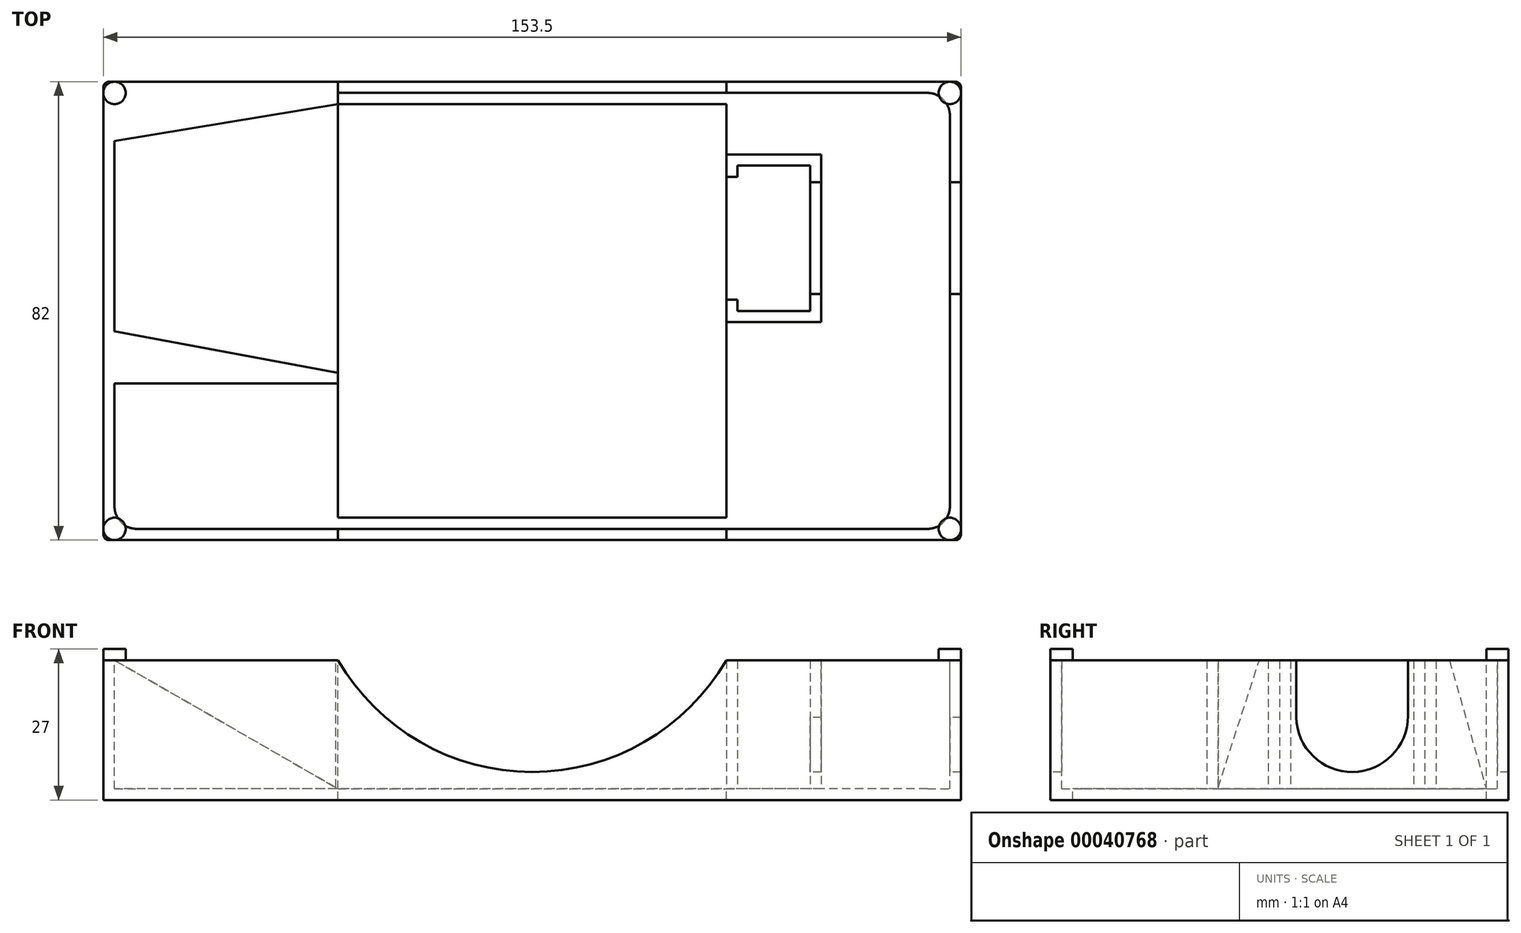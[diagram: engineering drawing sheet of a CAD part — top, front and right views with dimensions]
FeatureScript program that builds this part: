
annotation { "Feature Type Name" : "Feature", "Feature Type Description" : "" }
export const myFeature = defineFeature(function(context is Context, id is Id, definition is map)
    precondition{}
    {
        {
            var Q0;
            Q0=qCreatedBy(makeId("Top.planeOp"),FACE);
            var sketch = newSketch(context, id + "F0", { "sketchPlane" : qUnion([Q0])});
            skLineSegment(sketch, "E0.rect.bottom", {"start": v(76.75, -41) * mm, "end": v(-76.75, -41) * mm});
            skLineSegment(sketch, "E0.rect.top", {"start": v(76.75, 41) * mm, "end": v(-76.75, 41) * mm});
            skLineSegment(sketch, "E0.rect.left", {"start": v(76.75, -41) * mm, "end": v(76.75, 41) * mm});
            skLineSegment(sketch, "E0.rect.right", {"start": v(-76.75, -41) * mm, "end": v(-76.75, 41) * mm});
            skPoint(sketch, "E0.rect.middle", {"position": v(0, 0) * mm});
            skSolve(sketch);
        }
        {
            var Q0;
            Q0 = qSketchRegion(id + "F0", true);
            extrude(context, id + "F1", {"entities" : qUnion([Q0]), "depth" : 25 * mm});
        }
        {
            var Q0;
            Q0=makeQuery(id+"F1.opExtrude","CAP_FACE",FACE,{"disambiguationData":[OSD([sQuery(id+"F0.wireOp",EDGE,"E0.rect.bottom"),sQuery(id+"F0.wireOp",EDGE,"E0.rect.top"),sQuery(id+"F0.wireOp",EDGE,"E0.rect.left"),sQuery(id+"F0.wireOp",EDGE,"E0.rect.right")])],"isStart":false});
            var sketch = newSketch(context, id + "F2", { "sketchPlane" : qUnion([Q0])});
            skLineSegment(sketch, "E1.rect.bottom", {"start": v(74.75, -39) * mm, "end": v(-74.75, -39) * mm});
            skLineSegment(sketch, "E1.rect.top", {"start": v(74.75, 39) * mm, "end": v(-74.75, 39) * mm});
            skLineSegment(sketch, "E1.rect.left", {"start": v(74.75, -39) * mm, "end": v(74.75, 39) * mm});
            skLineSegment(sketch, "E1.rect.right", {"start": v(-74.75, -39) * mm, "end": v(-74.75, 39) * mm});
            skPoint(sketch, "E1.rect.middle", {"position": v(0, 0) * mm});
            skLineSegment(sketch, "E2", {"start": v(74.75, 0) * mm, "end": v(76.75, 0) * mm, "construction": true});
            skLineSegment(sketch, "E3", {"start": v(0, -39) * mm, "end": v(0, -41) * mm, "construction": true});
            skSolve(sketch);
        }
        {
            var Q0;
            Q0 = qSketchRegion(id + "F2", true);
            extrude(context, id + "F3", {"entities" : qUnion([Q0]), "operationType" : NewBodyOperationType.REMOVE, "oppositeDirection" : true, "depth" : 23 * mm});
        }
        {
            var Q0;
            Q0=makeQuery(id+"F3.boolean.opBoolean","COPY",FACE,{"derivedFrom":makeQuery(id+"F3.opExtrude","SWEPT_FACE",FACE,{"disambiguationData":[OSD([sQuery(id+"F2.wireOp",EDGE,"E1.rect.top")])]})});
            var sketch = newSketch(context, id + "F4", { "sketchPlane" : qUnion([Q0])});
            skLineSegment(sketch, "E4", {"start": v(-74.75, 25) * mm, "end": v(-34.75, 2) * mm});
            skLineSegment(sketch, "E5", {"start": v(-34.75, 2) * mm, "end": v(-74.75, 2) * mm});
            skLineSegment(sketch, "E6", {"start": v(-74.75, 2) * mm, "end": v(-74.75, 25) * mm});
            skSolve(sketch);
        }
        {
            var Q0;
            Q0 = qSketchRegion(id + "F4", true);
            extrude(context, id + "F5", {"entities" : qUnion([Q0]), "operationType" : NewBodyOperationType.ADD, "depth" : 50 * mm});
        }
        {
            var Q0;
            Q0=makeQuery(id+"F3.boolean.opBoolean","COPY",FACE,{"derivedFrom":makeQuery(id+"F3.opExtrude","CAP_FACE",FACE,{"disambiguationData":[OSD([sQuery(id+"F2.wireOp",EDGE,"E1.rect.bottom"),sQuery(id+"F2.wireOp",EDGE,"E1.rect.top"),sQuery(id+"F2.wireOp",EDGE,"E1.rect.left"),sQuery(id+"F2.wireOp",EDGE,"E1.rect.right")])],"isStart":false})});
            var sketch = newSketch(context, id + "F6", { "sketchPlane" : qUnion([Q0])});
            skLineSegment(sketch, "E7.bottom", {"start": v(-34.75, -11) * mm, "end": v(-74.75, -11) * mm});
            skLineSegment(sketch, "E7.top", {"start": v(-34.75, -13) * mm, "end": v(-74.75, -13) * mm});
            skLineSegment(sketch, "E7.left", {"start": v(-34.75, -11) * mm, "end": v(-34.75, -13) * mm});
            skLineSegment(sketch, "E7.right", {"start": v(-74.75, -11) * mm, "end": v(-74.75, -13) * mm});
            skSolve(sketch);
        }
        {
            var Q0;
            Q0 = qSketchRegion(id + "F6", true);
            extrude(context, id + "F7", {"entities" : qUnion([Q0]), "operationType" : NewBodyOperationType.ADD, "depth" : 23 * mm});
        }
        {
            var Q0;
            Q0=makeQuery(id+"F3.boolean.opBoolean","COPY",FACE,{"derivedFrom":makeQuery(id+"F3.opExtrude","CAP_FACE",FACE,{"disambiguationData":[OSD([sQuery(id+"F2.wireOp",EDGE,"E1.rect.bottom"),sQuery(id+"F2.wireOp",EDGE,"E1.rect.top"),sQuery(id+"F2.wireOp",EDGE,"E1.rect.left"),sQuery(id+"F2.wireOp",EDGE,"E1.rect.right")])],"isStart":false})});
            var sketch = newSketch(context, id + "F8", { "sketchPlane" : qUnion([Q0])});
            skLineSegment(sketch, "E8.rect.bottom", {"start": v(-34.75, 37) * mm, "end": v(34.75, 37) * mm});
            skLineSegment(sketch, "E8.rect.top", {"start": v(-34.75, -37) * mm, "end": v(34.75, -37) * mm});
            skLineSegment(sketch, "E8.rect.left", {"start": v(-34.75, 37) * mm, "end": v(-34.75, -37) * mm});
            skLineSegment(sketch, "E8.rect.right", {"start": v(34.75, 37) * mm, "end": v(34.75, -37) * mm});
            skPoint(sketch, "E8.rect.middle", {"position": v(0, 0) * mm});
            skLineSegment(sketch, "E9", {"start": v(0, 37) * mm, "end": v(0, 39) * mm, "construction": true});
            skSolve(sketch);
        }
        {
            var Q0;
            Q0 = qSketchRegion(id + "F8", true);
            extrude(context, id + "F9", {"entities" : qUnion([Q0]), "operationType" : NewBodyOperationType.REMOVE, "endBound" : BoundingType.THROUGH_ALL, "oppositeDirection" : true, "depth" : 25 * mm});
        }
        {
            var Q0;
            Q0=makeQuery(id+"F5.opExtrude","SWEPT_FACE",FACE,{"disambiguationData":[OSD([sQuery(id+"F4.wireOp",EDGE,"E4")])]});
            var sketch = newSketch(context, id + "F10", { "sketchPlane" : qUnion([Q0])});
            skLineSegment(sketch, "E10", {"start": v(-31.12, 37) * mm, "end": v(-77.26, 30.41) * mm});
            skLineSegment(sketch, "E11", {"start": v(-77.26, 30.41) * mm, "end": v(-77.26, 39) * mm});
            skLineSegment(sketch, "E12", {"start": v(-77.26, 39) * mm, "end": v(-31.12, 39) * mm});
            skLineSegment(sketch, "E13", {"start": v(-31.12, 39) * mm, "end": v(-31.12, 37) * mm});
            skLineSegment(sketch, "E14", {"start": v(-31.12, 13) * mm, "end": v(-31.12, 13) * mm});
            skPoint(sketch, "E14.endSnap0", {"position": v(-31.12, 13) * mm});
            skLineSegment(sketch, "E15.MirrorCS", {"start": v(-31.55, -11) * mm, "end": v(-77.57, -3.58) * mm});
            skLineSegment(sketch, "E16.MirrorCS", {"start": v(-77.57, -3.58) * mm, "end": v(-77.72, -12.17) * mm});
            skLineSegment(sketch, "E17.MirrorCS", {"start": v(-77.72, -12.17) * mm, "end": v(-31.59, -13) * mm});
            skLineSegment(sketch, "E18.MirrorCS", {"start": v(-31.59, -13) * mm, "end": v(-31.55, -11) * mm});
            skLineSegment(sketch, "E19", {"start": v(-77.26, 30.41) * mm, "end": v(-77.57, -3.58) * mm, "construction": true});
            skLineSegment(sketch, "E20", {"start": v(-77.26, 14) * mm, "end": v(-31.12, 13) * mm, "construction": true});
            skSolve(sketch);
        }
        {
            var Q0;
            Q0=makeQuery(id+"F7.boolean.opBoolean","MERGE",FACE,{"derivedFrom":[makeQuery(id+"F1.opExtrude","CAP_FACE",FACE,{"disambiguationData":[OSD([sQuery(id+"F0.wireOp",EDGE,"E0.rect.bottom"),sQuery(id+"F0.wireOp",EDGE,"E0.rect.top"),sQuery(id+"F0.wireOp",EDGE,"E0.rect.left"),sQuery(id+"F0.wireOp",EDGE,"E0.rect.right")])],"isStart":false}),makeQuery(id+"F7.opExtrude","CAP_FACE",FACE,{"disambiguationData":[OSD([sQuery(id+"F6.wireOp",EDGE,"E7.bottom"),sQuery(id+"F6.wireOp",EDGE,"E7.top"),sQuery(id+"F6.wireOp",EDGE,"E7.left"),sQuery(id+"F6.wireOp",EDGE,"E7.right")])],"isStart":false})]});
            var sketch = newSketch(context, id + "F11", { "sketchPlane" : qUnion([Q0])});
            skLineSegment(sketch, "E21.0.0", {"start": v(-74.75, 30.41) * mm, "end": v(-34.75, 37) * mm});
            skLineSegment(sketch, "E21.0.1", {"start": v(-34.75, 37) * mm, "end": v(-34.75, 39) * mm});
            skLineSegment(sketch, "E21.0.2", {"start": v(-34.75, 39) * mm, "end": v(-74.75, 39) * mm});
            skLineSegment(sketch, "E21.0.3", {"start": v(-74.75, 39) * mm, "end": v(-74.75, 30.41) * mm});
            skLineSegment(sketch, "E22.0.0", {"start": v(-35.12, -11) * mm, "end": v(-35.12, -11) * mm});
            skLineSegment(sketch, "E22.0.1", {"start": v(-35.12, -11) * mm, "end": v(-74.75, -3.63) * mm});
            skLineSegment(sketch, "E22.0.2", {"start": v(-74.75, -3.63) * mm, "end": v(-74.75, -11) * mm});
            skLineSegment(sketch, "E22.0.3", {"start": v(-74.75, -11) * mm, "end": v(-35.12, -11) * mm});
            skSolve(sketch);
        }
        {
            var Q0;
            Q0 = qSketchRegion(id + "F11", true);
            extrude(context, id + "F12", {"entities" : qUnion([Q0]), "operationType" : NewBodyOperationType.ADD, "oppositeDirection" : true, "depth" : 25 * mm});
        }
        {
            var Q0;
            Q0=makeQuery(id+"F12.boolean.opBoolean","MERGE",FACE,{"derivedFrom":[makeQuery(id+"F7.boolean.opBoolean","MERGE",FACE,{"derivedFrom":[makeQuery(id+"F1.opExtrude","CAP_FACE",FACE,{"disambiguationData":[OSD([sQuery(id+"F0.wireOp",EDGE,"E0.rect.bottom"),sQuery(id+"F0.wireOp",EDGE,"E0.rect.top"),sQuery(id+"F0.wireOp",EDGE,"E0.rect.left"),sQuery(id+"F0.wireOp",EDGE,"E0.rect.right")])],"isStart":false}),makeQuery(id+"F7.opExtrude","CAP_FACE",FACE,{"disambiguationData":[OSD([sQuery(id+"F6.wireOp",EDGE,"E7.bottom"),sQuery(id+"F6.wireOp",EDGE,"E7.top"),sQuery(id+"F6.wireOp",EDGE,"E7.left"),sQuery(id+"F6.wireOp",EDGE,"E7.right")])],"isStart":false})]}),makeQuery(id+"F12.opExtrude","CAP_FACE",FACE,{"disambiguationData":[OSD([sQuery(id+"F11.wireOp",EDGE,"E21.0.0"),sQuery(id+"F11.wireOp",EDGE,"E21.0.1"),sQuery(id+"F11.wireOp",EDGE,"E21.0.2"),sQuery(id+"F11.wireOp",EDGE,"E21.0.3")])],"isStart":true}),makeQuery(id+"F12.opExtrude","CAP_FACE",FACE,{"disambiguationData":[OSD([sQuery(id+"F11.wireOp",EDGE,"80184698-4208-4d28-adc6-4ba6be5a86be.0.0"),sQuery(id+"F11.wireOp",EDGE,"80184698-4208-4d28-adc6-4ba6be5a86be.0.1"),sQuery(id+"F11.wireOp",EDGE,"80184698-4208-4d28-adc6-4ba6be5a86be.0.2")])],"isStart":true})]});
            var sketch = newSketch(context, id + "F13", { "sketchPlane" : qUnion([Q0])});
            skPoint(sketch, "E23.oppositeSnap0", {"position": v(-74.75, 13.4) * mm});
            skLineSegment(sketch, "E23.bottom", {"start": v(-76.75, 41) * mm, "end": v(-49.14, 41) * mm, "construction": true});
            skLineSegment(sketch, "E23.top", {"start": v(-76.75, 13.4) * mm, "end": v(-49.14, 13.4) * mm, "construction": true});
            skLineSegment(sketch, "E23.left", {"start": v(-76.75, 41) * mm, "end": v(-76.75, 13.4) * mm, "construction": true});
            skLineSegment(sketch, "E23.right", {"start": v(-49.14, 41) * mm, "end": v(-49.14, 13.4) * mm, "construction": true});
            skPoint(sketch, "E24", {"position": v(-49.14, 13.4) * mm});
            skSolve(sketch);
        }
        {
            var Q0;
            Q0=makeQuery(id+"F3.boolean.opBoolean","COPY",FACE,{"derivedFrom":makeQuery(id+"F3.opExtrude","CAP_FACE",FACE,{"disambiguationData":[OSD([sQuery(id+"F2.wireOp",EDGE,"E1.rect.bottom"),sQuery(id+"F2.wireOp",EDGE,"E1.rect.top"),sQuery(id+"F2.wireOp",EDGE,"E1.rect.left"),sQuery(id+"F2.wireOp",EDGE,"E1.rect.right")])],"isStart":false})});
            var sketch = newSketch(context, id + "F14", { "sketchPlane" : qUnion([Q0])});
            skLineSegment(sketch, "E25.bottom", {"start": v(49.75, 26) * mm, "end": v(51.75, 26) * mm});
            skLineSegment(sketch, "E25.top", {"start": v(49.75, 0) * mm, "end": v(51.75, 0) * mm});
            skLineSegment(sketch, "E25.left", {"start": v(49.75, 26) * mm, "end": v(49.75, 0) * mm});
            skLineSegment(sketch, "E25.right", {"start": v(51.75, 26) * mm, "end": v(51.75, 0) * mm});
            skLineSegment(sketch, "E26.bottom", {"start": v(51.75, 0) * mm, "end": v(34.75, 0) * mm});
            skLineSegment(sketch, "E26.top", {"start": v(51.75, -2) * mm, "end": v(34.75, -2) * mm});
            skLineSegment(sketch, "E26.left", {"start": v(51.75, 0) * mm, "end": v(51.75, -2) * mm});
            skLineSegment(sketch, "E26.right", {"start": v(34.75, 0) * mm, "end": v(34.75, -2) * mm});
            skLineSegment(sketch, "E27.bottom", {"start": v(34.75, 0) * mm, "end": v(36.75, 0) * mm});
            skLineSegment(sketch, "E27.top", {"start": v(34.75, 2) * mm, "end": v(36.75, 2) * mm});
            skLineSegment(sketch, "E27.left", {"start": v(34.75, 0) * mm, "end": v(34.75, 2) * mm});
            skLineSegment(sketch, "E27.right", {"start": v(36.75, 0) * mm, "end": v(36.75, 2) * mm});
            skPoint(sketch, "E28.0", {"position": v(-34.75, 13) * mm});
            skLineSegment(sketch, "E29", {"start": v(-34.75, 13) * mm, "end": v(34.75, 13) * mm, "construction": true});
            skLineSegment(sketch, "E30", {"start": v(34.75, 13) * mm, "end": v(49.75, 13) * mm, "construction": true});
            skLineSegment(sketch, "E31.bottom", {"start": v(51.75, 28) * mm, "end": v(34.75, 28) * mm});
            skLineSegment(sketch, "E31.top", {"start": v(51.75, 26) * mm, "end": v(34.75, 26) * mm});
            skLineSegment(sketch, "E31.left", {"start": v(51.75, 28) * mm, "end": v(51.75, 26) * mm});
            skLineSegment(sketch, "E31.right", {"start": v(34.75, 28) * mm, "end": v(34.75, 26) * mm});
            skLineSegment(sketch, "E32.MirrorCS", {"start": v(34.75, 24) * mm, "end": v(36.75, 24) * mm});
            skLineSegment(sketch, "E33.MirrorCS", {"start": v(34.75, 26) * mm, "end": v(34.75, 24) * mm});
            skLineSegment(sketch, "E34.MirrorCS", {"start": v(36.75, 26) * mm, "end": v(36.75, 24) * mm});
            skSolve(sketch);
        }
        {
            var Q0;
            Q0 = qSketchRegion(id + "F14", true);
            extrude(context, id + "F15", {"entities" : qUnion([Q0]), "operationType" : NewBodyOperationType.ADD, "depth" : 23 * mm});
        }
        {
            var Q0;
            Q0=makeQuery(id+"F15.opExtrude","SWEPT_FACE",FACE,{"disambiguationData":[OSD([sQuery(id+"F14.wireOp",EDGE,"E25.left")])]});
            var sketch = newSketch(context, id + "F16", { "sketchPlane" : qUnion([Q0])});
            skLineSegment(sketch, "E35", {"start": v(-23, 25) * mm, "end": v(-3, 25) * mm});
            skLineSegment(sketch, "E36", {"start": v(-23, 25) * mm, "end": v(-23, 15) * mm});
            skLineSegment(sketch, "E37", {"start": v(-13, 25) * mm, "end": v(-13, 15) * mm, "construction": true});
            skLineSegment(sketch, "E38.MirrorCS", {"start": v(-3, 25) * mm, "end": v(-3, 14.8) * mm});
            skPoint(sketch, "E39", {"position": v(-13, 25) * mm});
            skArc(sketch, "E40", {"start": v(-23, 15) * mm, "mid": v(-13.1, 5) * mm, "end": v(-3, 14.8) * mm});
            skSolve(sketch);
        }
        {
            var Q0;
            Q0 = qSketchRegion(id + "F16", true);
            extrude(context, id + "F17", {"entities" : qUnion([Q0]), "operationType" : NewBodyOperationType.REMOVE, "endBound" : BoundingType.THROUGH_ALL, "oppositeDirection" : true, "depth" : 25 * mm});
        }
        {
            var Q0;
            Q0=makeQuery(id+"F1.opExtrude","SWEPT_FACE",FACE,{"disambiguationData":[OSD([sQuery(id+"F0.wireOp",EDGE,"E0.rect.bottom")])]});
            var sketch = newSketch(context, id + "F18", { "sketchPlane" : qUnion([Q0])});
            skPoint(sketch, "E41.0", {"position": v(-34.75, 25) * mm});
            skPoint(sketch, "E42.0", {"position": v(34.75, 25) * mm});
            skArc(sketch, "E43", {"start": v(-34.75, 25) * mm, "mid": v(0, 5) * mm, "end": v(34.75, 25) * mm});
            skLineSegment(sketch, "E44", {"start": v(0, 5) * mm, "end": v(0, 0) * mm, "construction": true});
            skLineSegment(sketch, "E45", {"start": v(-34.75, 25) * mm, "end": v(34.75, 25) * mm});
            skSolve(sketch);
        }
        {
            var Q0;
            Q0 = qSketchRegion(id + "F18", true);
            extrude(context, id + "F19", {"entities" : qUnion([Q0]), "operationType" : NewBodyOperationType.REMOVE, "endBound" : BoundingType.THROUGH_ALL, "oppositeDirection" : true, "depth" : 25 * mm});
        }
        {
            var Q0;
            Q0=makeQuery(id+"F13.imprint","IMPRINT",FACE,{"disambiguationData":[TD([[makeQuery(id+"F13.imprint","IMPRINT",EDGE,{"derivedFrom":makeQuery(id+"F1.opExtrude","CAP_EDGE",EDGE,{"disambiguationData":[OSD([sQuery(id+"F0.wireOp",EDGE,"E0.rect.bottom")])],"isStart":false})}),-1.0]])]});
            var sketch = newSketch(context, id + "F20", { "sketchPlane" : qUnion([Q0])});
            skLineSegment(sketch, "E46.rect.bottom", {"start": v(-74.75, -39) * mm, "end": v(74.75, -39) * mm, "construction": true});
            skLineSegment(sketch, "E46.rect.top", {"start": v(-74.75, 39) * mm, "end": v(74.75, 39) * mm, "construction": true});
            skLineSegment(sketch, "E46.rect.left", {"start": v(-74.75, -39) * mm, "end": v(-74.75, 39) * mm, "construction": true});
            skLineSegment(sketch, "E46.rect.right", {"start": v(74.75, -39) * mm, "end": v(74.75, 39) * mm, "construction": true});
            skPoint(sketch, "E46.rect.middle", {"position": v(0, 0) * mm});
            skPoint(sketch, "E47.0", {"position": v(-74.75, -39) * mm});
            skCircle(sketch, "E48", {"center": v(-74.75, 39) * mm, "radius": 2 * mm});
            skCircle(sketch, "E49", {"center": v(74.75, 39) * mm, "radius": 2 * mm});
            skCircle(sketch, "E50", {"center": v(-74.75, -39) * mm, "radius": 2 * mm});
            skCircle(sketch, "E51", {"center": v(74.75, -39) * mm, "radius": 2 * mm});
            skSolve(sketch);
        }
        {
            var Q0;
            Q0 = qSketchRegion(id + "F20", true);
            extrude(context, id + "F21", {"entities" : qUnion([Q0]), "operationType" : NewBodyOperationType.ADD, "depth" : 2 * mm});
        }
        {
            var Q0;
            Q0=makeQuery(id+"F3.boolean.opBoolean","COPY",EDGE,{"derivedFrom":makeQuery(id+"F3.opExtrude","SWEPT_EDGE",EDGE,{"disambiguationData":[OSD([sQuery(id+"F2.wireOp",EDGE,"E1.rect.bottom"),sQuery(id+"F2.wireOp",EDGE,"E1.rect.right")])]})});
            var Q1;
            Q1=makeQuery(id+"F3.boolean.opBoolean","COPY",EDGE,{"derivedFrom":makeQuery(id+"F3.opExtrude","SWEPT_EDGE",EDGE,{"disambiguationData":[OSD([sQuery(id+"F2.wireOp",EDGE,"E1.rect.top"),sQuery(id+"F2.wireOp",EDGE,"E1.rect.left")])]})});
            var Q2;
            Q2=makeQuery(id+"F3.boolean.opBoolean","COPY",EDGE,{"derivedFrom":makeQuery(id+"F3.opExtrude","SWEPT_EDGE",EDGE,{"disambiguationData":[OSD([sQuery(id+"F2.wireOp",EDGE,"E1.rect.bottom"),sQuery(id+"F2.wireOp",EDGE,"E1.rect.left")])]})});
            var Q3;
            Q3=makeQuery(id+"F15.opExtrude","CAP_EDGE",EDGE,{"disambiguationData":[OSD([sQuery(id+"F14.wireOp",EDGE,"E26.top")])],"isStart":true});
            var Q4;
            Q4=makeQuery(id+"F15.opExtrude","CAP_EDGE",EDGE,{"disambiguationData":[OSD([sQuery(id+"F14.wireOp",EDGE,"E31.bottom")])],"isStart":true});
            fillet(context, id + "F22", {"entities" : qUnion([Q0, Q1, Q2, Q3, Q4]), "radius" : 4 * mm, "tangentPropagation" : true, "allowEdgeOverflow" : false});
        }
        {
            var Q0;
            Q0=makeQuery(id+"F1.opExtrude","SWEPT_EDGE",EDGE,{"disambiguationData":[OSD([sQuery(id+"F0.wireOp",EDGE,"E0.rect.bottom"),sQuery(id+"F0.wireOp",EDGE,"E0.rect.left")])]});
            var Q1;
            Q1=makeQuery(id+"F1.opExtrude","SWEPT_EDGE",EDGE,{"disambiguationData":[OSD([sQuery(id+"F0.wireOp",EDGE,"E0.rect.bottom"),sQuery(id+"F0.wireOp",EDGE,"E0.rect.right")])]});
            var Q2;
            Q2=makeQuery(id+"F1.opExtrude","SWEPT_EDGE",EDGE,{"disambiguationData":[OSD([sQuery(id+"F0.wireOp",EDGE,"E0.rect.top"),sQuery(id+"F0.wireOp",EDGE,"E0.rect.right")])]});
            var Q3;
            Q3=makeQuery(id+"F1.opExtrude","SWEPT_EDGE",EDGE,{"disambiguationData":[OSD([sQuery(id+"F0.wireOp",EDGE,"E0.rect.top"),sQuery(id+"F0.wireOp",EDGE,"E0.rect.left")])]});
            fillet(context, id + "F23", {"entities" : qUnion([Q0, Q1, Q2, Q3]), "radius" : 1 * mm, "tangentPropagation" : true, "allowEdgeOverflow" : false});
        }
    });
